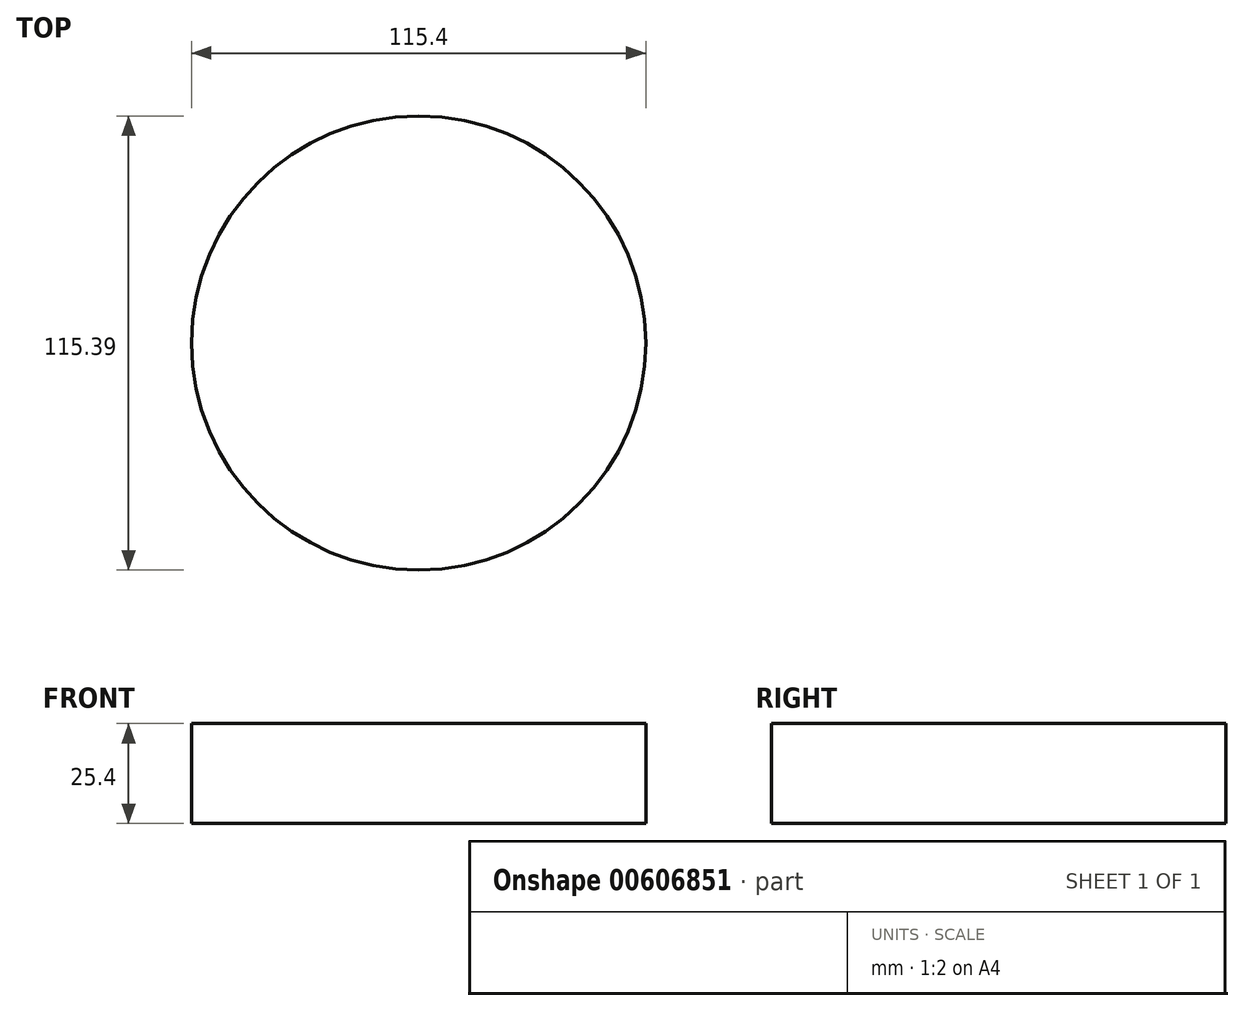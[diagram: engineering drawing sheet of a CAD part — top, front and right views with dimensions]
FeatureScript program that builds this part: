
annotation { "Feature Type Name" : "Feature", "Feature Type Description" : "" }
export const myFeature = defineFeature(function(context is Context, id is Id, definition is map)
    precondition{}
    {
        {
            var Q0;
            Q0=qCreatedBy(makeId("Top.planeOp"),FACE);
            var sketch = newSketch(context, id + "F0", { "sketchPlane" : qUnion([Q0])});
            skCircle(sketch, "E0", {"center": v(-45.04, -25.66) * mm, "radius": 57.7 * mm});
            skSolve(sketch);
        }
        {
            var Q0;
            Q0=makeQuery(id+"F0.imprint","IMPRINT",FACE,{"disambiguationData":[TD([[makeQuery(id+"F0.imprint","IMPRINT",EDGE,{"derivedFrom":sQuery(id+"F0.wireOp",EDGE,"E0")}),1.0]])]});
            extrude(context, id + "F1", {"entities" : qUnion([Q0]), "depth" : 25.4 * mm, "offsetDistance" : 25.4 * mm});
        }
    });
